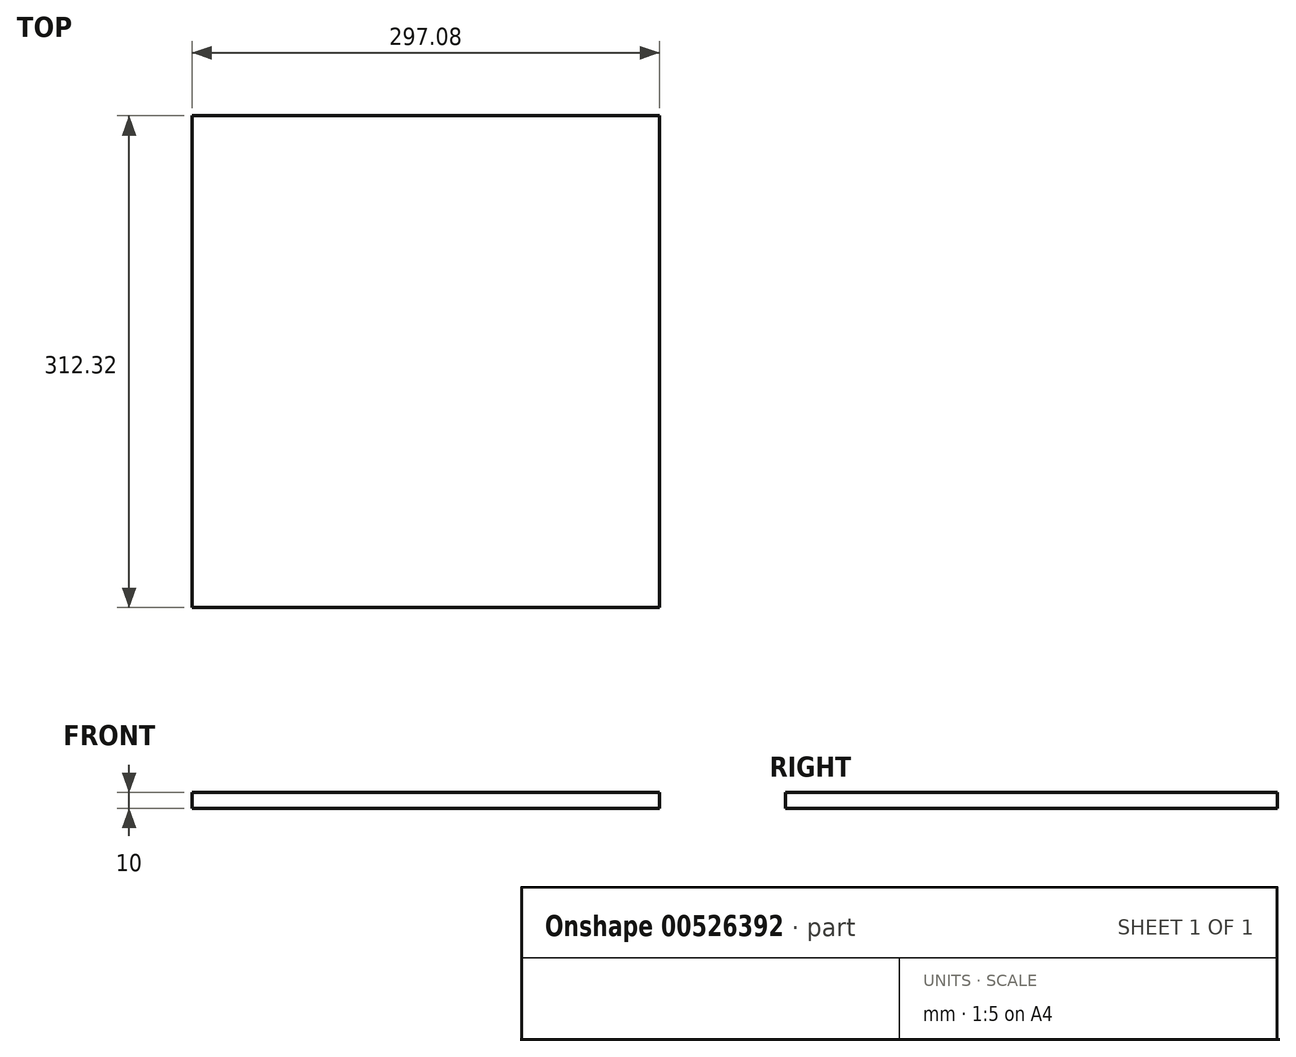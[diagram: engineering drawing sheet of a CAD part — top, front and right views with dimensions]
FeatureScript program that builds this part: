
annotation { "Feature Type Name" : "Feature", "Feature Type Description" : "" }
export const myFeature = defineFeature(function(context is Context, id is Id, definition is map)
    precondition{}
    {
        {
            var Q0;
            Q0=qCreatedBy(makeId("Top.planeOp"),FACE);
            var sketch = newSketch(context, id + "F0", { "sketchPlane" : qUnion([Q0])});
            skLineSegment(sketch, "E0.bottom", {"start": v(148.54, -156.16) * mm, "end": v(-148.54, -156.16) * mm});
            skLineSegment(sketch, "E0.top", {"start": v(148.54, 156.16) * mm, "end": v(-148.54, 156.16) * mm});
            skLineSegment(sketch, "E0.left", {"start": v(148.54, -156.16) * mm, "end": v(148.54, 156.16) * mm});
            skLineSegment(sketch, "E0.right", {"start": v(-148.54, -156.16) * mm, "end": v(-148.54, 156.16) * mm});
            skPoint(sketch, "E0.middle", {"position": v(0, 0) * mm});
            skSolve(sketch);
        }
        {
            var Q0;
            Q0=makeQuery(id+"F0.imprint","IMPRINT",FACE,{"disambiguationData":[TD([[makeQuery(id+"F0.imprint","IMPRINT",EDGE,{"derivedFrom":sQuery(id+"F0.wireOp",EDGE,"E0.bottom")}),-1.0]])]});
            extrude(context, id + "F1", {"entities" : qUnion([Q0]), "depth" : 10 * mm, "offsetDistance" : 25 * mm});
        }
    });
